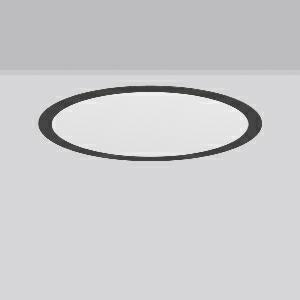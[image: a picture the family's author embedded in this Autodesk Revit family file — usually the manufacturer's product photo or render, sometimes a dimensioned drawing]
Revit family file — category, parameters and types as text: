
# Revit family: toledo_flat__round_e_901812_0031_2_730_0582
name_source: partatom
category: Lighting Fixtures
units: mm (PartAtom-declared; Revit-internal decimal feet)

## family parameters
Cut with Voids When Loaded = No
Host = Face
Light Source = No
Part Type = Normal
Room Calculation Point = No
Round Connector Dimension = Use Diameter
Shared = No

## types (1)
- TuneableWhite 827 (1 x LED Modul 827, 3150 lm, 2700)
    Apparent Load = 26 VA
    CIE Flux Codes = 47 79 96 100 100
    Color Rendering = 80
    Color Temperature = 2700
    Default Elevation = 1800 mm
    Description = Series: TOLEDO FLAT+ round
Flexible round recessed multifunction downlight. Housing: sheet steel, powder-coated. Luminaire frame: aluminium, powder-coated. Light guide and diffuser made of non-yellowing PMMA, opal matt. LED backlight technology for homogeneous illumination of the entire light-emitting surface. Tunable white dynamically adjustable from 2700 K to 6500 K. Suitable for Recessed ceiling mounting. Ceiling installation with spring system. Can be directly covered with thermal insulation material (applies only to the lower lumen levels). Including separate LED converter with connecting cable 250 mm. With Casambi smart+free Bluetooth control for wireless network and operation using Android / iOS devices, free app available for download. Surface mounted housing as accessory for all sizes. 
Colour: anthracite metallic (DB703)
Diameter: 470 mm
Height: 2 mm
Cut-out diameter: 457 mm
Recess height: 70 mm
Luminaire: recess height: 41 mm
Lamp: LED
Socket: without socket
Colour temperature: 2700K - 6500K
Colour rendering index (CRI): 80
System power: 26 W
Rated luminous flux: 3150 lm
Luminous efficiency: 121 lm/W
System power 2: 26 W
Rated luminous flux 2: 3300 lm
Luminous efficiency 2: 127 lm/W
System power 3: 26 W
Rated luminous flux 3: 3300 lm
Luminous efficiency 3: 127 lm/W
Control gear: Dimmable Bluetooth converter
Protection class: II
Type of protection: IP 54
    Height = 0 mm  [stored 0 ft]
    Lamp = 1 x LED Modul 827
    Lamp Light Flux = 3150 lm
    Lamp count = 1
    Length = 470 mm
    Lifetime = 50000 h
    Luminous efficacy = 121 lm/W
    Manufacturer = RZB
    ModVariant = No
    Model = 901812.0031.2.730
    Mounting Place = Ceiling
    Mounting Type = Recessed
    Number of Poles = 1
    OnlyDefault = Yes
    Power Factor = 1
    Product Name = TOLEDO FLAT+ round E
    Product group = Recessed downlights
    ProductGroupID = 402
    Protection Class = Protection class II
    Protection Degree = Degree of protection
    RLX_Detail_Level = 1
    RLX_Emergency_Light_Flux = 0 lm
    RLX_Emergency_Type = 0
    RLX_Emergency_Type_DB = No
    RlxData = <blob elided: 40213 chars, md5=527c0a0c>
    Socket = socket
    Standby Power = 0 W
    System Light Flux = 3150 lm
    System Power = 26 W
    Type Comments = TuneableWhite 827
    Type Image = 901812.0031.jpg
    URL = http://relux.com
    VarID = tuneablewhite_827
    Voltage = 0 V
    Weight = 0.00 kg
    Width = 0 mm  [stored 0 ft]

note: [stored X ft] marks values corroborated as IEEE doubles in the binary element streams (Revit-internal decimal feet)

## geometry (parser evidence)
native form markers: Blend x4, Sweep x9
no freeform markers — native parametric forms only
